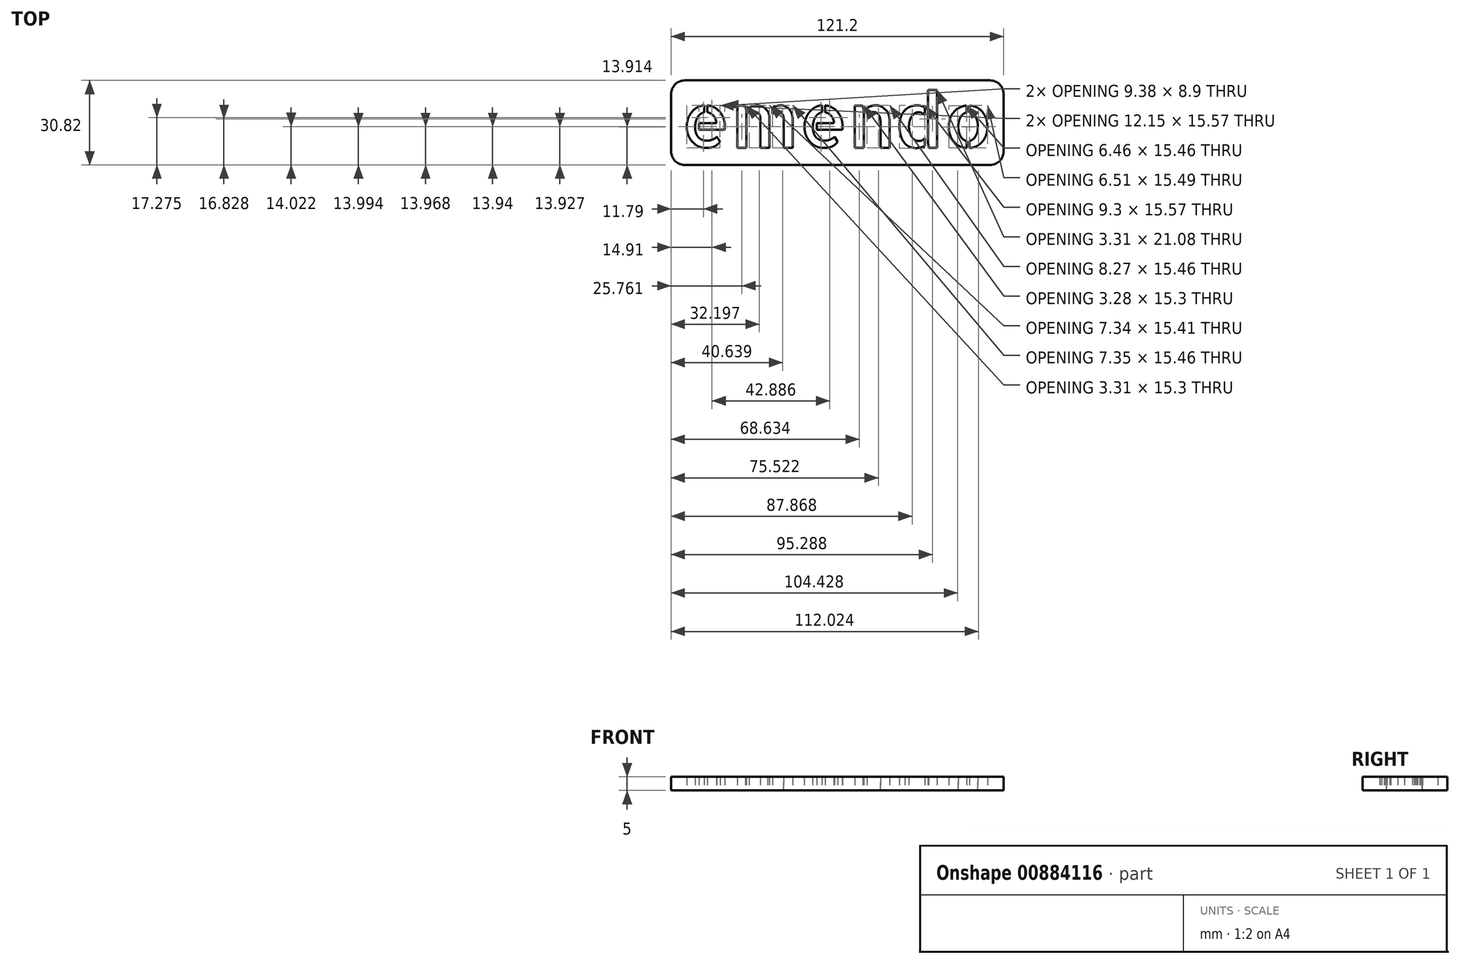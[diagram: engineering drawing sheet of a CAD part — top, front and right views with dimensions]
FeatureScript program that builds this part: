
annotation { "Feature Type Name" : "Feature", "Feature Type Description" : "" }
export const myFeature = defineFeature(function(context is Context, id is Id, definition is map)
    precondition{}
    {
        {
            var Q0;
            Q0=qCreatedBy(makeId("Top.planeOp"),FACE);
            var sketch = newSketch(context, id + "F0", { "sketchPlane" : qUnion([Q0])});
            skLineSegment(sketch, "E0.bottom", {"start": v(-3.76, 4.53) * mm, "end": v(117.44, 4.53) * mm});
            skLineSegment(sketch, "E0.top", {"start": v(-3.76, -26.3) * mm, "end": v(117.44, -26.3) * mm});
            skLineSegment(sketch, "E0.left", {"start": v(-3.76, 4.53) * mm, "end": v(-3.76, -26.3) * mm});
            skLineSegment(sketch, "E0.right", {"start": v(117.44, 4.53) * mm, "end": v(117.44, -26.3) * mm});
            skSolve(sketch);
        }
        {
            var Q0;
            Q0 = qSketchRegion(id + "F0", true);
            extrude(context, id + "F1", {"entities" : qUnion([Q0]), "depth" : 5 * mm, "offsetDistance" : 25 * mm});
        }
        {
            var Q0;
            Q0=qCreatedBy(makeId("Top.planeOp"),FACE);
            var sketch = newSketch(context, id + "F2", { "sketchPlane" : qUnion([Q0])});
            skText(sketch, "E1", { "text": "emendo", "fontName": "AllertaStencil-Regular.ttf"});
            const initialGuessF2  = {"E1": [0, -0.02, 1, 0, 0.02]};
            skSetInitialGuess(sketch, initialGuessF2);
            skSolve(sketch);
        }
        {
            var Q0;
            Q0 = qSketchRegion(id + "F2", true);
            extrude(context, id + "F3", {"entities" : qUnion([Q0]), "operationType" : NewBodyOperationType.REMOVE, "endBound" : BoundingType.THROUGH_ALL, "depth" : 25 * mm, "offsetDistance" : 25 * mm});
        }
        {
            var Q0;
            Q0=makeQuery(id+"F1.opExtrude","SWEPT_EDGE",EDGE,{"disambiguationData":[OSD([sQuery(id+"F0.wireOp",EDGE,"E0.top"),sQuery(id+"F0.wireOp",EDGE,"E0.left")])]});
            var Q1;
            Q1=makeQuery(id+"F1.opExtrude","SWEPT_EDGE",EDGE,{"disambiguationData":[OSD([sQuery(id+"F0.wireOp",EDGE,"E0.top"),sQuery(id+"F0.wireOp",EDGE,"E0.right")])]});
            var Q2;
            Q2=makeQuery(id+"F1.opExtrude","SWEPT_EDGE",EDGE,{"disambiguationData":[OSD([sQuery(id+"F0.wireOp",EDGE,"E0.bottom"),sQuery(id+"F0.wireOp",EDGE,"E0.right")])]});
            var Q3;
            Q3=makeQuery(id+"F1.opExtrude","SWEPT_EDGE",EDGE,{"disambiguationData":[OSD([sQuery(id+"F0.wireOp",EDGE,"E0.bottom"),sQuery(id+"F0.wireOp",EDGE,"E0.left")])]});
            fillet(context, id + "F4", {"entities" : qUnion([Q0, Q1, Q2, Q3]), "radius" : 5 * mm, "tangentPropagation" : true, "allowEdgeOverflow" : false});
        }
    });
